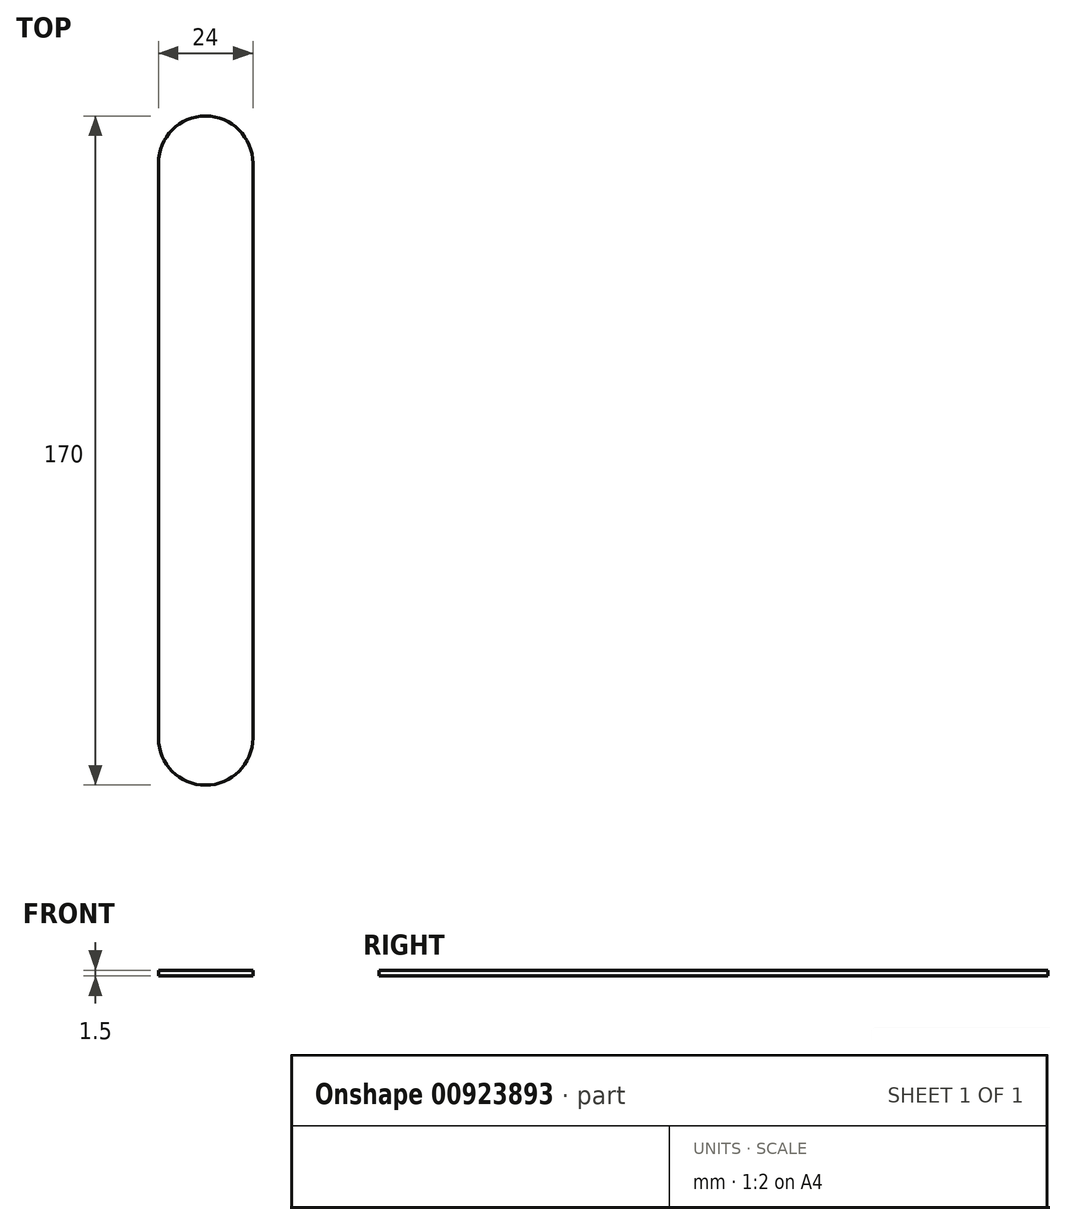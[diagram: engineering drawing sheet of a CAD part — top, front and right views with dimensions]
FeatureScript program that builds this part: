
annotation { "Feature Type Name" : "Feature", "Feature Type Description" : "" }
export const myFeature = defineFeature(function(context is Context, id is Id, definition is map)
    precondition{}
    {
        {
            var Q0;
            Q0=qCreatedBy(makeId("Top.planeOp"),FACE);
            var sketch = newSketch(context, id + "F0", { "sketchPlane" : qUnion([Q0])});
            skArc(sketch, "E0", {"start": v(12, 73) * mm, "mid": v(0, 85) * mm, "end": v(-12, 73) * mm});
            skArc(sketch, "E1", {"start": v(-12, -73) * mm, "mid": v(0, -85) * mm, "end": v(12, -73) * mm});
            skLineSegment(sketch, "E2.left", {"start": v(12, -73) * mm, "end": v(12, 73) * mm});
            skLineSegment(sketch, "E2.right", {"start": v(-12, -73) * mm, "end": v(-12, 73) * mm});
            skPoint(sketch, "E2.middle", {"position": v(0, 0) * mm});
            skPoint(sketch, "E3", {"position": v(0, 85) * mm});
            skPoint(sketch, "E4", {"position": v(0, -85) * mm});
            skSolve(sketch);
        }
        {
            var Q0;
            Q0 = qSketchRegion(id + "F0", true);
            extrude(context, id + "F1", {"entities" : qUnion([Q0]), "depth" : 1.5 * mm, "offsetDistance" : 25 * mm});
        }
    });
